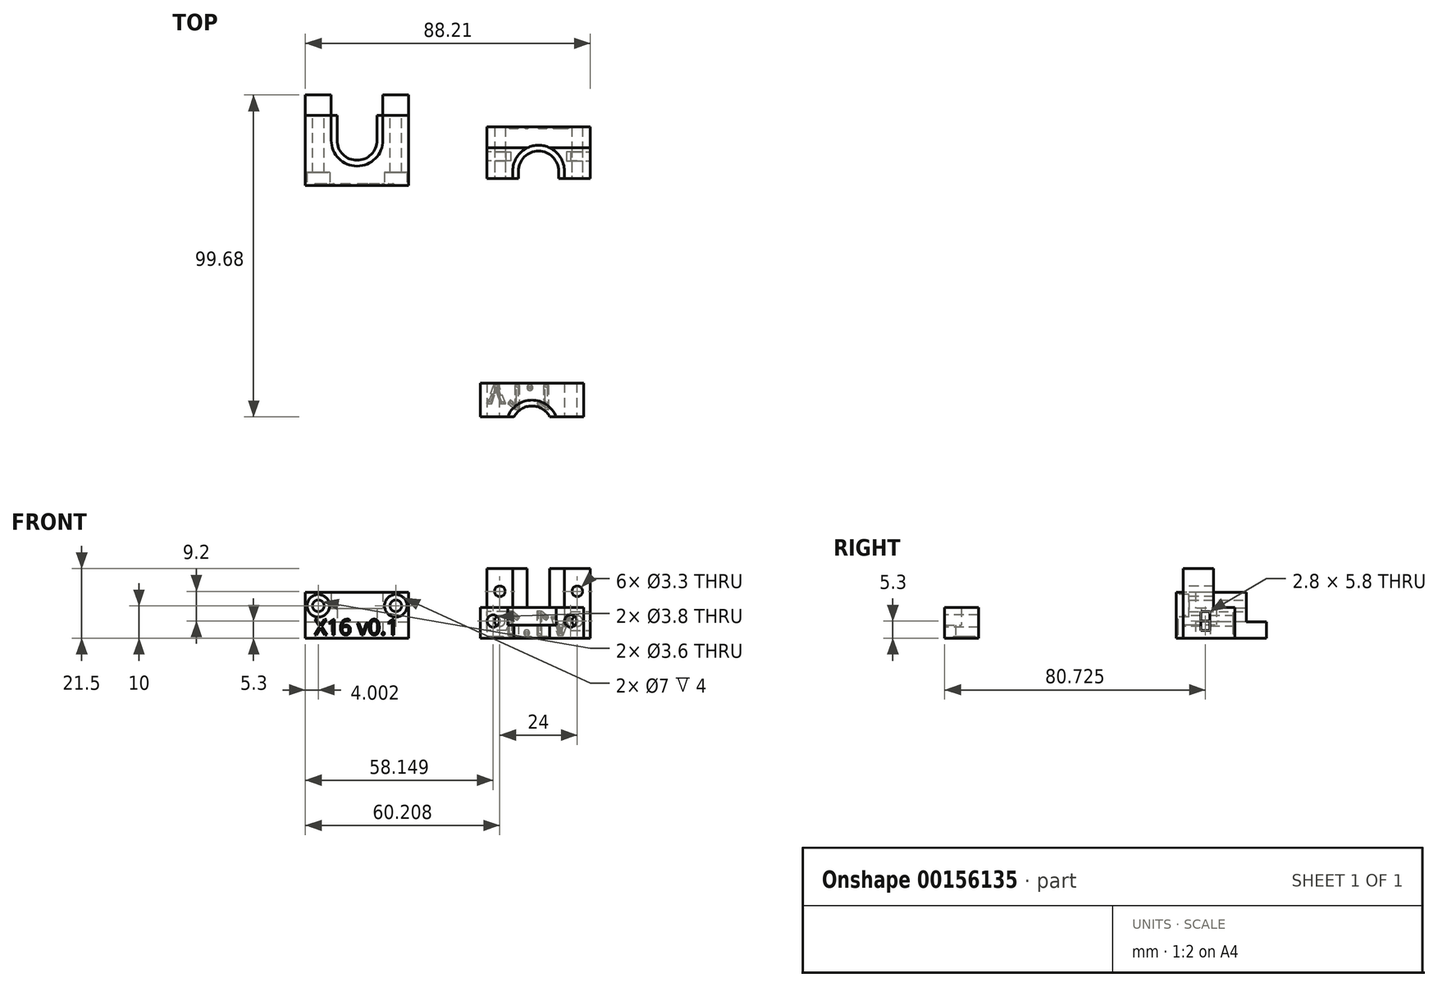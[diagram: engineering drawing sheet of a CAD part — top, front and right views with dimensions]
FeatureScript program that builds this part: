
annotation { "Feature Type Name" : "Feature", "Feature Type Description" : "" }
export const myFeature = defineFeature(function(context is Context, id is Id, definition is map)
    precondition{}
    {
        {
            var Q0;
            Q0=qCreatedBy(makeId("Top.planeOp"),FACE);
            var sketch = newSketch(context, id + "F0", { "sketchPlane" : qUnion([Q0])});
            skLineSegment(sketch, "E0.top", {"start": v(-38.58, -28.92) * mm, "end": v(-6.58, -28.92) * mm});
            skLineSegment(sketch, "E0.left", {"start": v(-38.58, -0.92) * mm, "end": v(-38.58, -28.92) * mm});
            skLineSegment(sketch, "E0.right", {"start": v(-6.58, -0.92) * mm, "end": v(-6.58, -28.92) * mm});
            skLineSegment(sketch, "E1", {"start": v(-38.58, -0.92) * mm, "end": v(-30.58, -0.92) * mm});
            skLineSegment(sketch, "E2", {"start": v(-14.58, -0.92) * mm, "end": v(-6.58, -0.92) * mm});
            skLineSegment(sketch, "E3.top", {"start": v(-22.58, -22.92) * mm, "end": v(-22.58, -22.92) * mm});
            skLineSegment(sketch, "E3.left", {"start": v(-30.58, -0.92) * mm, "end": v(-30.58, -14.92) * mm});
            skLineSegment(sketch, "E3.right", {"start": v(-14.58, -0.92) * mm, "end": v(-14.58, -14.92) * mm});
            skPoint(sketch, "E4.visualSharp", {"position": v(-30.58, -22.92) * mm});
            skArc(sketch, "E4.filletArc", {"start": v(-30.58, -14.92) * mm, "mid": v(-28.24, -20.58) * mm, "end": v(-22.58, -22.92) * mm});
            skPoint(sketch, "E5.visualSharp", {"position": v(-14.58, -22.92) * mm});
            skArc(sketch, "E5.filletArc", {"start": v(-22.58, -22.92) * mm, "mid": v(-16.92, -20.58) * mm, "end": v(-14.58, -14.92) * mm});
            skSolve(sketch);
        }
        {
            var Q0;
            Q0 = qSketchRegion(id + "F0", true);
            extrude(context, id + "F1", {"entities" : qUnion([Q0]), "depth" : 5 * mm});
        }
        {
            var Q0;
            Q0=makeQuery(id+"F1.opExtrude","CAP_FACE",FACE,{"disambiguationData":[OSD([sQuery(id+"F0.wireOp",EDGE,"E0.top"),sQuery(id+"F0.wireOp",EDGE,"E0.left"),sQuery(id+"F0.wireOp",EDGE,"E0.right"),sQuery(id+"F0.wireOp",EDGE,"E1"),sQuery(id+"F0.wireOp",EDGE,"E2"),sQuery(id+"F0.wireOp",EDGE,"E3.left"),sQuery(id+"F0.wireOp",EDGE,"E3.right"),sQuery(id+"F0.wireOp",EDGE,"E4.filletArc"),sQuery(id+"F0.wireOp",EDGE,"E5.filletArc")])],"isStart":false});
            var sketch = newSketch(context, id + "F2", { "sketchPlane" : qUnion([Q0])});
            skLineSegment(sketch, "E6", {"start": v(-6.58, -28.92) * mm, "end": v(-6.58, -7.22) * mm});
            skLineSegment(sketch, "E7", {"start": v(-6.58, -28.92) * mm, "end": v(-38.58, -28.92) * mm});
            skLineSegment(sketch, "E8", {"start": v(-38.58, -28.92) * mm, "end": v(-38.58, -7.22) * mm});
            skPoint(sketch, "E9.orphan", {"position": v(-30.58, -0.92) * mm});
            skPoint(sketch, "E10.orphan", {"position": v(-14.58, -0.92) * mm});
            skLineSegment(sketch, "E11", {"start": v(-38.58, -7.22) * mm, "end": v(-28.78, -7.22) * mm});
            skLineSegment(sketch, "E12", {"start": v(-16.38, -7.22) * mm, "end": v(-6.58, -7.22) * mm});
            skLineSegment(sketch, "E13.left", {"start": v(-28.78, -7.22) * mm, "end": v(-28.78, -14.92) * mm});
            skLineSegment(sketch, "E13.right", {"start": v(-16.38, -7.22) * mm, "end": v(-16.38, -14.92) * mm});
            skArc(sketch, "E14", {"start": v(-28.78, -14.92) * mm, "mid": v(-22.58, -21.12) * mm, "end": v(-16.38, -14.92) * mm});
            skSolve(sketch);
        }
        {
            var Q0;
            Q0 = qSketchRegion(id + "F2", true);
            extrude(context, id + "F3", {"entities" : qUnion([Q0]), "operationType" : NewBodyOperationType.ADD, "depth" : 4.2 * mm});
        }
        {
            var Q0;
            Q0=makeQuery(id+"F3.opExtrude","CAP_FACE",FACE,{"disambiguationData":[OSD([sQuery(id+"F2.wireOp",EDGE,"E6"),sQuery(id+"F2.wireOp",EDGE,"E7"),sQuery(id+"F2.wireOp",EDGE,"E8"),sQuery(id+"F2.wireOp",EDGE,"E11"),sQuery(id+"F2.wireOp",EDGE,"E12"),sQuery(id+"F2.wireOp",EDGE,"E13.left"),sQuery(id+"F2.wireOp",EDGE,"E13.right"),sQuery(id+"F2.wireOp",EDGE,"E14")])],"isStart":false});
            var sketch = newSketch(context, id + "F4", { "sketchPlane" : qUnion([Q0])});
            skLineSegment(sketch, "E15.0", {"start": v(-38.58, -7.22) * mm, "end": v(-38.58, -28.92) * mm});
            skLineSegment(sketch, "E16.0", {"start": v(-38.58, -28.92) * mm, "end": v(-6.58, -28.92) * mm});
            skLineSegment(sketch, "E17.0", {"start": v(-6.58, -7.22) * mm, "end": v(-6.58, -28.92) * mm});
            skPoint(sketch, "E18.orphan", {"position": v(-38.58, -0.92) * mm});
            skPoint(sketch, "E19.orphan", {"position": v(-6.58, -0.92) * mm});
            skPoint(sketch, "E20.0.start.orphan", {"position": v(-28.78, -14.92) * mm});
            skPoint(sketch, "E21.0.end.orphan", {"position": v(-16.38, -14.92) * mm});
            skPoint(sketch, "E22.0.start.orphan", {"position": v(-16.38, -7.22) * mm});
            skPoint(sketch, "E23.0.end.orphan", {"position": v(-28.78, -7.22) * mm});
            skLineSegment(sketch, "E24.0", {"start": v(-30.58, -7.22) * mm, "end": v(-30.58, -14.92) * mm});
            skLineSegment(sketch, "E25.0", {"start": v(-14.58, -7.22) * mm, "end": v(-14.58, -14.92) * mm});
            skArc(sketch, "E26.0", {"start": v(-22.58, -22.92) * mm, "mid": v(-16.92, -20.58) * mm, "end": v(-14.58, -14.92) * mm});
            skArc(sketch, "E27.0", {"start": v(-30.58, -14.92) * mm, "mid": v(-28.24, -20.58) * mm, "end": v(-22.58, -22.92) * mm});
            skLineSegment(sketch, "E28", {"start": v(-38.58, -7.22) * mm, "end": v(-30.58, -7.22) * mm});
            skLineSegment(sketch, "E29", {"start": v(-6.58, -7.22) * mm, "end": v(-14.58, -7.22) * mm});
            skPoint(sketch, "E30.orphan", {"position": v(-30.58, -0.92) * mm});
            skPoint(sketch, "E31.orphan", {"position": v(-14.58, -0.92) * mm});
            skSolve(sketch);
        }
        {
            var Q0;
            Q0 = qSketchRegion(id + "F4", true);
            extrude(context, id + "F5", {"entities" : qUnion([Q0]), "operationType" : NewBodyOperationType.ADD, "depth" : 5 * mm});
        }
        {
            var Q0;
            Q0=makeQuery(id+"F5.boolean.opBoolean","MERGE",FACE,{"derivedFrom":[makeQuery(id+"F3.opExtrude","SWEPT_FACE",FACE,{"disambiguationData":[OSD([sQuery(id+"F2.wireOp",EDGE,"E12")])]}),makeQuery(id+"F5.opExtrude","SWEPT_FACE",FACE,{"disambiguationData":[OSD([sQuery(id+"F4.wireOp",EDGE,"E29")])]})]});
            var sketch = newSketch(context, id + "F6", { "sketchPlane" : qUnion([Q0])});
            skLineSegment(sketch, "E32.0", {"start": v(14.58, 0) * mm, "end": v(6.58, 0) * mm});
            skLineSegment(sketch, "E33", {"start": v(6.58, 0) * mm, "end": v(6.58, 10) * mm});
            skLineSegment(sketch, "E34.0", {"start": v(38.58, 0) * mm, "end": v(30.58, 0) * mm});
            skLineSegment(sketch, "E35", {"start": v(30.58, 0) * mm, "end": v(30.58, 10) * mm});
            skLineSegment(sketch, "E36", {"start": v(6.58, 10) * mm, "end": v(10.58, 10) * mm});
            skLineSegment(sketch, "E37", {"start": v(30.58, 10) * mm, "end": v(34.58, 10) * mm});
            skCircle(sketch, "E38", {"center": v(10.58, 10) * mm, "radius": 1.8 * mm});
            skCircle(sketch, "E39", {"center": v(34.58, 10) * mm, "radius": 1.8 * mm});
            skSolve(sketch);
        }
        {
            var Q0;
            Q0 = qSketchRegion(id + "F6", true);
            extrude(context, id + "F7", {"entities" : qUnion([Q0]), "operationType" : NewBodyOperationType.REMOVE, "oppositeDirection" : true, "depth" : 25 * mm});
        }
        {
            var Q0;
            Q0=qCreatedBy(makeId("Top.planeOp"),FACE);
            var sketch = newSketch(context, id + "F8", { "sketchPlane" : qUnion([Q0])});
            skLineSegment(sketch, "E40.bottom", {"start": v(17.63, -10.78) * mm, "end": v(49.63, -10.78) * mm});
            skLineSegment(sketch, "E40.left", {"start": v(17.63, -10.78) * mm, "end": v(17.63, -26.78) * mm});
            skLineSegment(sketch, "E40.right", {"start": v(49.63, -10.78) * mm, "end": v(49.63, -26.78) * mm});
            skLineSegment(sketch, "E41", {"start": v(17.63, -26.78) * mm, "end": v(27.43, -26.78) * mm});
            skLineSegment(sketch, "E42", {"start": v(49.63, -26.78) * mm, "end": v(39.83, -26.78) * mm});
            skLineSegment(sketch, "E43", {"start": v(27.43, -26.78) * mm, "end": v(27.43, -24.48) * mm});
            skLineSegment(sketch, "E44", {"start": v(39.83, -26.78) * mm, "end": v(39.83, -24.48) * mm});
            skArc(sketch, "E45", {"start": v(39.83, -24.48) * mm, "mid": v(33.63, -18.28) * mm, "end": v(27.43, -24.48) * mm});
            skSolve(sketch);
        }
        {
            var Q0;
            Q0 = qSketchRegion(id + "F8", true);
            extrude(context, id + "F9", {"entities" : qUnion([Q0]), "depth" : 4.2 * mm});
        }
        {
            var Q0;
            Q0=makeQuery(id+"F9.opExtrude","CAP_FACE",FACE,{"disambiguationData":[OSD([sQuery(id+"F8.wireOp",EDGE,"E40.bottom"),sQuery(id+"F8.wireOp",EDGE,"E40.left"),sQuery(id+"F8.wireOp",EDGE,"E40.right"),sQuery(id+"F8.wireOp",EDGE,"E41"),sQuery(id+"F8.wireOp",EDGE,"E42"),sQuery(id+"F8.wireOp",EDGE,"E43"),sQuery(id+"F8.wireOp",EDGE,"E44"),sQuery(id+"F8.wireOp",EDGE,"E45")])],"isStart":false});
            var sketch = newSketch(context, id + "F10", { "sketchPlane" : qUnion([Q0])});
            skLineSegment(sketch, "E46", {"start": v(49.63, -26.78) * mm, "end": v(41.63, -26.78) * mm});
            skLineSegment(sketch, "E47", {"start": v(41.63, -26.78) * mm, "end": v(41.63, -24.48) * mm});
            skLineSegment(sketch, "E48", {"start": v(17.63, -26.78) * mm, "end": v(25.63, -26.78) * mm});
            skLineSegment(sketch, "E49", {"start": v(25.63, -26.78) * mm, "end": v(25.63, -24.48) * mm});
            skArc(sketch, "E50", {"start": v(41.63, -24.48) * mm, "mid": v(33.63, -16.48) * mm, "end": v(25.63, -24.48) * mm});
            skLineSegment(sketch, "E51.0", {"start": v(17.63, -10.78) * mm, "end": v(17.63, -26.78) * mm});
            skLineSegment(sketch, "E52.0", {"start": v(17.63, -10.78) * mm, "end": v(49.63, -10.78) * mm});
            skLineSegment(sketch, "E53.0", {"start": v(49.63, -10.78) * mm, "end": v(49.63, -26.78) * mm});
            skSolve(sketch);
        }
        {
            var Q0;
            Q0 = qSketchRegion(id + "F10", true);
            extrude(context, id + "F11", {"entities" : qUnion([Q0]), "operationType" : NewBodyOperationType.ADD, "depth" : 17.3 * mm});
        }
        {
            var Q0;
            Q0=makeQuery(id+"F11.opExtrude","CAP_FACE",FACE,{"disambiguationData":[OSD([sQuery(id+"F10.wireOp",EDGE,"E46"),sQuery(id+"F10.wireOp",EDGE,"E47"),sQuery(id+"F10.wireOp",EDGE,"E48"),sQuery(id+"F10.wireOp",EDGE,"E49"),sQuery(id+"F10.wireOp",EDGE,"E50"),sQuery(id+"F10.wireOp",EDGE,"E51.0"),sQuery(id+"F10.wireOp",EDGE,"E52.0"),sQuery(id+"F10.wireOp",EDGE,"E53.0")])],"isStart":false});
            var sketch = newSketch(context, id + "F12", { "sketchPlane" : qUnion([Q0])});
            skLineSegment(sketch, "E54.bottom", {"start": v(17.63, -10.78) * mm, "end": v(49.63, -10.78) * mm});
            skLineSegment(sketch, "E54.top", {"start": v(17.63, -17.28) * mm, "end": v(49.63, -17.28) * mm});
            skLineSegment(sketch, "E54.left", {"start": v(17.63, -10.78) * mm, "end": v(17.63, -17.28) * mm});
            skLineSegment(sketch, "E54.right", {"start": v(49.63, -10.78) * mm, "end": v(49.63, -17.28) * mm});
            skSolve(sketch);
        }
        {
            var Q0;
            Q0 = qSketchRegion(id + "F12", true);
            extrude(context, id + "F13", {"entities" : qUnion([Q0]), "operationType" : NewBodyOperationType.REMOVE, "oppositeDirection" : true, "depth" : 12 * mm});
        }
        {
            var Q0;
            Q0=makeQuery(id+"F11.boolean.opBoolean","MERGE",FACE,{"derivedFrom":[makeQuery(id+"F9.opExtrude","SWEPT_FACE",FACE,{"disambiguationData":[OSD([sQuery(id+"F8.wireOp",EDGE,"E41")])]}),makeQuery(id+"F11.opExtrude","SWEPT_FACE",FACE,{"disambiguationData":[OSD([sQuery(id+"F10.wireOp",EDGE,"E48")])]})]});
            var sketch = newSketch(context, id + "F14", { "sketchPlane" : qUnion([Q0])});
            skLineSegment(sketch, "E55", {"start": v(17.63, 21.5) * mm, "end": v(17.63, 14.5) * mm, "construction": true});
            skLineSegment(sketch, "E56", {"start": v(17.63, 14.5) * mm, "end": v(21.63, 14.5) * mm, "construction": true});
            skLineSegment(sketch, "E57", {"start": v(21.63, 14.5) * mm, "end": v(45.63, 14.5) * mm, "construction": true});
            skLineSegment(sketch, "E58.0", {"start": v(49.63, 21.5) * mm, "end": v(49.63, 0) * mm, "construction": true});
            skLineSegment(sketch, "E59", {"start": v(45.63, 14.5) * mm, "end": v(49.63, 14.5) * mm, "construction": true});
            skLineSegment(sketch, "E60", {"start": v(45.63, 14.5) * mm, "end": v(45.63, 5.3) * mm, "construction": true});
            skLineSegment(sketch, "E61", {"start": v(45.63, 5.3) * mm, "end": v(21.63, 5.3) * mm, "construction": true});
            skCircle(sketch, "E62", {"center": v(21.63, 14.5) * mm, "radius": 1.65 * mm});
            skCircle(sketch, "E63", {"center": v(45.63, 14.5) * mm, "radius": 1.65 * mm});
            skCircle(sketch, "E64", {"center": v(45.63, 5.3) * mm, "radius": 1.65 * mm});
            skCircle(sketch, "E65", {"center": v(21.63, 5.3) * mm, "radius": 1.65 * mm});
            skSolve(sketch);
        }
        {
            var Q0;
            Q0 = qSketchRegion(id + "F14", true);
            extrude(context, id + "F15", {"entities" : qUnion([Q0]), "operationType" : NewBodyOperationType.REMOVE, "oppositeDirection" : true, "depth" : 25 * mm});
        }
        {
            var Q0;
            Q0=makeQuery(id+"F11.boolean.opBoolean","MERGE",FACE,{"derivedFrom":[makeQuery(id+"F9.opExtrude","SWEPT_FACE",FACE,{"disambiguationData":[OSD([sQuery(id+"F8.wireOp",EDGE,"E40.left")])]}),makeQuery(id+"F11.opExtrude","SWEPT_FACE",FACE,{"disambiguationData":[OSD([sQuery(id+"F10.wireOp",EDGE,"E51.0")])]})]});
            var sketch = newSketch(context, id + "F16", { "sketchPlane" : qUnion([Q0])});
            skLineSegment(sketch, "E66", {"start": v(26.78, 0) * mm, "end": v(21.28, 0) * mm});
            skLineSegment(sketch, "E67", {"start": v(21.28, 0) * mm, "end": v(21.28, 2.4) * mm});
            skLineSegment(sketch, "E68.bottom", {"start": v(21.28, 2.4) * mm, "end": v(18.48, 2.4) * mm});
            skLineSegment(sketch, "E68.top", {"start": v(21.28, 8.2) * mm, "end": v(18.48, 8.2) * mm});
            skLineSegment(sketch, "E68.left", {"start": v(21.28, 2.4) * mm, "end": v(21.28, 8.2) * mm});
            skLineSegment(sketch, "E68.right", {"start": v(18.48, 2.4) * mm, "end": v(18.48, 8.2) * mm});
            skSolve(sketch);
        }
        {
            var Q0;
            Q0 = qSketchRegion(id + "F16", true);
            extrude(context, id + "F17", {"entities" : qUnion([Q0]), "operationType" : NewBodyOperationType.REMOVE, "oppositeDirection" : true, "depth" : 6 * mm});
        }
        {
            var Q0;
            Q0=makeQuery(id+"F11.boolean.opBoolean","MERGE",FACE,{"derivedFrom":[makeQuery(id+"F9.opExtrude","SWEPT_FACE",FACE,{"disambiguationData":[OSD([sQuery(id+"F8.wireOp",EDGE,"E40.right")])]}),makeQuery(id+"F11.opExtrude","SWEPT_FACE",FACE,{"disambiguationData":[OSD([sQuery(id+"F10.wireOp",EDGE,"E53.0")])]})]});
            var sketch = newSketch(context, id + "F18", { "sketchPlane" : qUnion([Q0])});
            skLineSegment(sketch, "E69.0", {"start": v(-21.28, 8.2) * mm, "end": v(-18.48, 8.2) * mm});
            skLineSegment(sketch, "E70.0", {"start": v(-21.28, 2.4) * mm, "end": v(-21.28, 8.2) * mm});
            skLineSegment(sketch, "E71.0", {"start": v(-21.28, 2.4) * mm, "end": v(-18.48, 2.4) * mm});
            skLineSegment(sketch, "E72.0", {"start": v(-18.48, 2.4) * mm, "end": v(-18.48, 8.2) * mm});
            skSolve(sketch);
        }
        {
            var Q0;
            Q0 = qSketchRegion(id + "F18", true);
            extrude(context, id + "F19", {"entities" : qUnion([Q0]), "operationType" : NewBodyOperationType.REMOVE, "oppositeDirection" : true, "depth" : 6 * mm});
        }
        {
            var Q0;
            Q0=makeQuery(id+"F17.boolean.opBoolean","COPY",FACE,{"derivedFrom":makeQuery(id+"F17.opExtrude","SWEPT_FACE",FACE,{"disambiguationData":[OSD([sQuery(id+"F16.wireOp",EDGE,"E68.left")])]})});
            var sketch = newSketch(context, id + "F20", { "sketchPlane" : qUnion([Q0])});
            skLineSegment(sketch, "E73", {"start": v(-23.63, 8.2) * mm, "end": v(-23.63, 2.4) * mm});
            skLineSegment(sketch, "E74", {"start": v(-23.63, 2.4) * mm, "end": v(-24.98, 5.3) * mm});
            skLineSegment(sketch, "E75", {"start": v(-24.98, 5.3) * mm, "end": v(-23.63, 8.2) * mm});
            skLineSegment(sketch, "E76.0", {"start": v(-43.63, 2.4) * mm, "end": v(-43.63, 8.2) * mm});
            skLineSegment(sketch, "E77", {"start": v(-43.63, 8.2) * mm, "end": v(-42.27, 5.3) * mm});
            skLineSegment(sketch, "E78", {"start": v(-42.27, 5.3) * mm, "end": v(-43.63, 2.4) * mm});
            skSolve(sketch);
        }
        {
            var Q0;
            Q0 = qSketchRegion(id + "F20", true);
            extrude(context, id + "F21", {"entities" : qUnion([Q0]), "operationType" : NewBodyOperationType.REMOVE, "depth" : 2.8 * mm});
        }
        {
            var Q0;
            Q0=makeQuery(id+"F11.boolean.opBoolean","MERGE",FACE,{"derivedFrom":[makeQuery(id+"F9.opExtrude","SWEPT_FACE",FACE,{"disambiguationData":[OSD([sQuery(id+"F8.wireOp",EDGE,"E40.bottom")])]}),makeQuery(id+"F11.opExtrude","SWEPT_FACE",FACE,{"disambiguationData":[OSD([sQuery(id+"F10.wireOp",EDGE,"E52.0")])]})]});
            var sketch = newSketch(context, id + "F22", { "sketchPlane" : qUnion([Q0])});
            skText(sketch, "E79", { "text": "v1.1", "fontName": "OpenSans-Bold.ttf"});
            const initialGuessF22  = {"E79": [-0.04342, 0.00088, 1, 0, 0.00757]};
            skSetInitialGuess(sketch, initialGuessF22);
            skSolve(sketch);
        }
        {
            var Q0;
            Q0 = qSketchRegion(id + "F22", true);
            extrude(context, id + "F23", {"entities" : qUnion([Q0]), "operationType" : NewBodyOperationType.REMOVE, "oppositeDirection" : true, "depth" : .5 * mm});
        }
        {
            var Q0;
            Q0=qCreatedBy(makeId("Top.planeOp"),FACE);
            var sketch = newSketch(context, id + "F24", { "sketchPlane" : qUnion([Q0])});
            skLineSegment(sketch, "E80.bottom", {"start": v(15.57, -90.1) * mm, "end": v(47.57, -90.1) * mm});
            skLineSegment(sketch, "E80.top", {"start": v(15.57, -100.6) * mm, "end": v(26.04, -100.6) * mm});
            skLineSegment(sketch, "E80.left", {"start": v(15.57, -90.1) * mm, "end": v(15.57, -100.6) * mm});
            skLineSegment(sketch, "E80.right", {"start": v(47.57, -90.1) * mm, "end": v(47.57, -100.6) * mm});
            skArc(sketch, "E81", {"start": v(37.1, -100.6) * mm, "mid": v(31.57, -97.2) * mm, "end": v(26.04, -100.6) * mm});
            skLineSegment(sketch, "E82.trimOffspring", {"start": v(37.1, -100.6) * mm, "end": v(47.57, -100.6) * mm});
            skPoint(sketch, "E83.start.orphan", {"position": v(31.57, -100.6) * mm});
            skSolve(sketch);
        }
        {
            var Q0;
            Q0 = qSketchRegion(id + "F24", true);
            extrude(context, id + "F25", {"entities" : qUnion([Q0]), "depth" : 4 * mm});
        }
        {
            var Q0;
            Q0=makeQuery(id+"F25.opExtrude","CAP_FACE",FACE,{"disambiguationData":[OSD([sQuery(id+"F24.wireOp",EDGE,"E80.bottom"),sQuery(id+"F24.wireOp",EDGE,"E80.top"),sQuery(id+"F24.wireOp",EDGE,"E80.left"),sQuery(id+"F24.wireOp",EDGE,"E80.right"),sQuery(id+"F24.wireOp",EDGE,"E81"),sQuery(id+"F24.wireOp",EDGE,"E82.trimOffspring")])],"isStart":false});
            var sketch = newSketch(context, id + "F26", { "sketchPlane" : qUnion([Q0])});
            skLineSegment(sketch, "E84.0", {"start": v(15.57, -90.1) * mm, "end": v(47.57, -90.1) * mm});
            skLineSegment(sketch, "E85.0", {"start": v(15.57, -90.1) * mm, "end": v(15.57, -100.6) * mm});
            skLineSegment(sketch, "E86.0", {"start": v(47.57, -90.1) * mm, "end": v(47.57, -100.6) * mm});
            skPoint(sketch, "E87.0", {"position": v(31.57, -103.4) * mm});
            skArc(sketch, "E88", {"start": v(39.06, -100.6) * mm, "mid": v(31.57, -95.4) * mm, "end": v(24.07, -100.6) * mm});
            skLineSegment(sketch, "E89", {"start": v(15.57, -100.6) * mm, "end": v(24.07, -100.6) * mm});
            skLineSegment(sketch, "E90", {"start": v(47.57, -100.6) * mm, "end": v(39.06, -100.6) * mm});
            skSolve(sketch);
        }
        {
            var Q0;
            Q0 = qSketchRegion(id + "F26", true);
            extrude(context, id + "F27", {"entities" : qUnion([Q0]), "operationType" : NewBodyOperationType.ADD, "depth" : 5.5 * mm});
        }
        {
            var Q0;
            Q0=makeQuery(id+"F27.boolean.opBoolean","MERGE",FACE,{"derivedFrom":[makeQuery(id+"F25.opExtrude","SWEPT_FACE",FACE,{"disambiguationData":[OSD([sQuery(id+"F24.wireOp",EDGE,"E80.top")])]}),makeQuery(id+"F27.opExtrude","SWEPT_FACE",FACE,{"disambiguationData":[OSD([sQuery(id+"F26.wireOp",EDGE,"E89")])]})]});
            var sketch = newSketch(context, id + "F28", { "sketchPlane" : qUnion([Q0])});
            skLineSegment(sketch, "E91", {"start": v(15.57, 9.5) * mm, "end": v(15.57, 5.3) * mm, "construction": true});
            skLineSegment(sketch, "E92", {"start": v(15.57, 5.3) * mm, "end": v(19.57, 5.3) * mm, "construction": true});
            skLineSegment(sketch, "E93", {"start": v(19.57, 5.3) * mm, "end": v(43.57, 5.3) * mm, "construction": true});
            skCircle(sketch, "E94", {"center": v(19.57, 5.3) * mm, "radius": 1.9 * mm});
            skCircle(sketch, "E95", {"center": v(43.57, 5.3) * mm, "radius": 1.9 * mm});
            skSolve(sketch);
        }
        {
            var Q0;
            Q0 = qSketchRegion(id + "F28", true);
            extrude(context, id + "F29", {"entities" : qUnion([Q0]), "operationType" : NewBodyOperationType.REMOVE, "oppositeDirection" : true, "depth" : 25 * mm});
        }
        {
            var Q0;
            Q0=makeQuery(id+"F25.opExtrude","CAP_FACE",FACE,{"disambiguationData":[OSD([sQuery(id+"F24.wireOp",EDGE,"E80.bottom"),sQuery(id+"F24.wireOp",EDGE,"E80.top"),sQuery(id+"F24.wireOp",EDGE,"E80.left"),sQuery(id+"F24.wireOp",EDGE,"E80.right"),sQuery(id+"F24.wireOp",EDGE,"E81"),sQuery(id+"F24.wireOp",EDGE,"E82.trimOffspring")])],"isStart":true});
            var sketch = newSketch(context, id + "F30", { "sketchPlane" : qUnion([Q0])});
            skText(sketch, "E96", { "text": "v1.1", "fontName": "OpenSans-Bold.ttf"});
            const initialGuessF30  = {"E96": [0.01747, 0.09077, 1, 0, 0.00757]};
            skSetInitialGuess(sketch, initialGuessF30);
            skSolve(sketch);
        }
        {
            var Q0;
            Q0 = qSketchRegion(id + "F30", true);
            extrude(context, id + "F31", {"entities" : qUnion([Q0]), "operationType" : NewBodyOperationType.REMOVE, "oppositeDirection" : true, "depth" : .5 * mm});
        }
        {
            var Q0;
            Q0=makeQuery(id+"F31.boolean.opBoolean","COPY",FACE,{"derivedFrom":makeQuery(id+"F31.opExtrude","CAP_FACE",FACE,{"disambiguationData":[OSD([sQuery(id+"F30.wireOp",EDGE,"E96.sketch_text.stroke-0"),sQuery(id+"F30.wireOp",EDGE,"E96.sketch_text.stroke-1"),sQuery(id+"F30.wireOp",EDGE,"E96.sketch_text.stroke-2"),sQuery(id+"F30.wireOp",EDGE,"E96.sketch_text.stroke-3"),sQuery(id+"F30.wireOp",EDGE,"E96.sketch_text.stroke-4"),sQuery(id+"F30.wireOp",EDGE,"E96.sketch_text.stroke-5"),sQuery(id+"F30.wireOp",EDGE,"E96.sketch_text.stroke-6"),sQuery(id+"F30.wireOp",EDGE,"E96.sketch_text.stroke-7"),sQuery(id+"F30.wireOp",EDGE,"E96.sketch_text.stroke-8"),sQuery(id+"F30.wireOp",EDGE,"E96.sketch_text.stroke-9")])],"isStart":false})});
            var Q1;
            Q1=makeQuery(id+"F31.boolean.opBoolean","COPY",FACE,{"derivedFrom":makeQuery(id+"F31.opExtrude","CAP_FACE",FACE,{"disambiguationData":[OSD([sQuery(id+"F30.wireOp",EDGE,"E96.sketch_text.stroke-10"),sQuery(id+"F30.wireOp",EDGE,"E96.sketch_text.stroke-11"),sQuery(id+"F30.wireOp",EDGE,"E96.sketch_text.stroke-12"),sQuery(id+"F30.wireOp",EDGE,"E96.sketch_text.stroke-13"),sQuery(id+"F30.wireOp",EDGE,"E96.sketch_text.stroke-14"),sQuery(id+"F30.wireOp",EDGE,"E96.sketch_text.stroke-15"),sQuery(id+"F30.wireOp",EDGE,"E96.sketch_text.stroke-16"),sQuery(id+"F30.wireOp",EDGE,"E96.sketch_text.stroke-17"),sQuery(id+"F30.wireOp",EDGE,"E96.sketch_text.stroke-18"),sQuery(id+"F30.wireOp",EDGE,"E96.sketch_text.stroke-19")])],"isStart":false})});
            var Q2;
            Q2=makeQuery(id+"F31.boolean.opBoolean","COPY",FACE,{"derivedFrom":makeQuery(id+"F31.opExtrude","CAP_FACE",FACE,{"disambiguationData":[OSD([sQuery(id+"F30.wireOp",EDGE,"E96.sketch_text.stroke-20"),sQuery(id+"F30.wireOp",EDGE,"E96.sketch_text.stroke-21"),sQuery(id+"F30.wireOp",EDGE,"E96.sketch_text.stroke-22"),sQuery(id+"F30.wireOp",EDGE,"E96.sketch_text.stroke-23"),sQuery(id+"F30.wireOp",EDGE,"E96.sketch_text.stroke-24"),sQuery(id+"F30.wireOp",EDGE,"E96.sketch_text.stroke-25"),sQuery(id+"F30.wireOp",EDGE,"E96.sketch_text.stroke-26"),sQuery(id+"F30.wireOp",EDGE,"E96.sketch_text.stroke-27")])],"isStart":false})});
            var Q3;
            Q3=makeQuery(id+"F31.boolean.opBoolean","COPY",FACE,{"derivedFrom":makeQuery(id+"F31.opExtrude","CAP_FACE",FACE,{"disambiguationData":[OSD([sQuery(id+"F30.wireOp",EDGE,"E96.sketch_text.stroke-28"),sQuery(id+"F30.wireOp",EDGE,"E96.sketch_text.stroke-29"),sQuery(id+"F30.wireOp",EDGE,"E96.sketch_text.stroke-30"),sQuery(id+"F30.wireOp",EDGE,"E96.sketch_text.stroke-31"),sQuery(id+"F30.wireOp",EDGE,"E96.sketch_text.stroke-32"),sQuery(id+"F30.wireOp",EDGE,"E96.sketch_text.stroke-33"),sQuery(id+"F30.wireOp",EDGE,"E96.sketch_text.stroke-34"),sQuery(id+"F30.wireOp",EDGE,"E96.sketch_text.stroke-35"),sQuery(id+"F30.wireOp",EDGE,"E96.sketch_text.stroke-36"),sQuery(id+"F30.wireOp",EDGE,"E96.sketch_text.stroke-37"),sQuery(id+"F30.wireOp",EDGE,"E96.sketch_text.stroke-38"),sQuery(id+"F30.wireOp",EDGE,"E96.sketch_text.stroke-39"),sQuery(id+"F30.wireOp",EDGE,"E96.sketch_text.stroke-40"),sQuery(id+"F30.wireOp",EDGE,"E96.sketch_text.stroke-41"),sQuery(id+"F30.wireOp",EDGE,"E96.sketch_text.stroke-42"),sQuery(id+"F30.wireOp",EDGE,"E96.sketch_text.stroke-43")])],"isStart":false})});
            chamfer(context, id + "F32", {"entities" : qUnion([Q0, Q1, Q2, Q3]), "width" : .5 * mm, "tangentPropagation" : true});
        }
        {
            var Q0;
            Q0=makeQuery(id+"F23.boolean.opBoolean","COPY",FACE,{"derivedFrom":makeQuery(id+"F23.opExtrude","CAP_FACE",FACE,{"disambiguationData":[OSD([sQuery(id+"F22.wireOp",EDGE,"E79.sketch_text.stroke-0"),sQuery(id+"F22.wireOp",EDGE,"E79.sketch_text.stroke-1"),sQuery(id+"F22.wireOp",EDGE,"E79.sketch_text.stroke-2"),sQuery(id+"F22.wireOp",EDGE,"E79.sketch_text.stroke-3"),sQuery(id+"F22.wireOp",EDGE,"E79.sketch_text.stroke-4"),sQuery(id+"F22.wireOp",EDGE,"E79.sketch_text.stroke-5"),sQuery(id+"F22.wireOp",EDGE,"E79.sketch_text.stroke-6"),sQuery(id+"F22.wireOp",EDGE,"E79.sketch_text.stroke-7"),sQuery(id+"F22.wireOp",EDGE,"E79.sketch_text.stroke-8"),sQuery(id+"F22.wireOp",EDGE,"E79.sketch_text.stroke-9")])],"isStart":false})});
            var Q1;
            Q1=makeQuery(id+"F23.boolean.opBoolean","COPY",FACE,{"derivedFrom":makeQuery(id+"F23.opExtrude","CAP_FACE",FACE,{"disambiguationData":[OSD([sQuery(id+"F22.wireOp",EDGE,"E79.sketch_text.stroke-10"),sQuery(id+"F22.wireOp",EDGE,"E79.sketch_text.stroke-11"),sQuery(id+"F22.wireOp",EDGE,"E79.sketch_text.stroke-12"),sQuery(id+"F22.wireOp",EDGE,"E79.sketch_text.stroke-13"),sQuery(id+"F22.wireOp",EDGE,"E79.sketch_text.stroke-14"),sQuery(id+"F22.wireOp",EDGE,"E79.sketch_text.stroke-15"),sQuery(id+"F22.wireOp",EDGE,"E79.sketch_text.stroke-16"),sQuery(id+"F22.wireOp",EDGE,"E79.sketch_text.stroke-17"),sQuery(id+"F22.wireOp",EDGE,"E79.sketch_text.stroke-18"),sQuery(id+"F22.wireOp",EDGE,"E79.sketch_text.stroke-19")])],"isStart":false})});
            var Q2;
            Q2=makeQuery(id+"F23.boolean.opBoolean","COPY",FACE,{"derivedFrom":makeQuery(id+"F23.opExtrude","CAP_FACE",FACE,{"disambiguationData":[OSD([sQuery(id+"F22.wireOp",EDGE,"E79.sketch_text.stroke-20"),sQuery(id+"F22.wireOp",EDGE,"E79.sketch_text.stroke-21"),sQuery(id+"F22.wireOp",EDGE,"E79.sketch_text.stroke-22"),sQuery(id+"F22.wireOp",EDGE,"E79.sketch_text.stroke-23"),sQuery(id+"F22.wireOp",EDGE,"E79.sketch_text.stroke-24"),sQuery(id+"F22.wireOp",EDGE,"E79.sketch_text.stroke-25"),sQuery(id+"F22.wireOp",EDGE,"E79.sketch_text.stroke-26"),sQuery(id+"F22.wireOp",EDGE,"E79.sketch_text.stroke-27")])],"isStart":false})});
            var Q3;
            Q3=makeQuery(id+"F23.boolean.opBoolean","COPY",FACE,{"derivedFrom":makeQuery(id+"F23.opExtrude","CAP_FACE",FACE,{"disambiguationData":[OSD([sQuery(id+"F22.wireOp",EDGE,"E79.sketch_text.stroke-28"),sQuery(id+"F22.wireOp",EDGE,"E79.sketch_text.stroke-29"),sQuery(id+"F22.wireOp",EDGE,"E79.sketch_text.stroke-30"),sQuery(id+"F22.wireOp",EDGE,"E79.sketch_text.stroke-31"),sQuery(id+"F22.wireOp",EDGE,"E79.sketch_text.stroke-32"),sQuery(id+"F22.wireOp",EDGE,"E79.sketch_text.stroke-33"),sQuery(id+"F22.wireOp",EDGE,"E79.sketch_text.stroke-34"),sQuery(id+"F22.wireOp",EDGE,"E79.sketch_text.stroke-35"),sQuery(id+"F22.wireOp",EDGE,"E79.sketch_text.stroke-36"),sQuery(id+"F22.wireOp",EDGE,"E79.sketch_text.stroke-37")])],"isStart":false})});
            chamfer(context, id + "F33", {"entities" : qUnion([Q0, Q1, Q2, Q3]), "width" : .5 * mm, "tangentPropagation" : true});
        }
        {
            var Q0;
            Q0=makeQuery(id+"F5.boolean.opBoolean","MERGE",FACE,{"derivedFrom":[makeQuery(id+"F3.boolean.opBoolean","MERGE",FACE,{"derivedFrom":[makeQuery(id+"F1.opExtrude","SWEPT_FACE",FACE,{"disambiguationData":[OSD([sQuery(id+"F0.wireOp",EDGE,"E0.top")])]}),makeQuery(id+"F3.opExtrude","SWEPT_FACE",FACE,{"disambiguationData":[OSD([sQuery(id+"F2.wireOp",EDGE,"E7")])]})]}),makeQuery(id+"F5.opExtrude","SWEPT_FACE",FACE,{"disambiguationData":[OSD([sQuery(id+"F4.wireOp",EDGE,"E16.0")])]})]});
            var sketch = newSketch(context, id + "F34", { "sketchPlane" : qUnion([Q0])});
            skCircle(sketch, "E97", {"center": v(-34.58, 10) * mm, "radius": 3.5 * mm});
            skCircle(sketch, "E98", {"center": v(-10.58, 10) * mm, "radius": 3.5 * mm});
            skSolve(sketch);
        }
        {
            var Q0;
            Q0=makeQuery(id+"F34.imprint","IMPRINT",FACE,{"disambiguationData":[TD([[makeQuery(id+"F34.imprint","IMPRINT",EDGE,{"derivedFrom":sQuery(id+"F34.wireOp",EDGE,"E97")}),1.0]])]});
            extrude(context, id + "F35", {"entities" : qUnion([Q0]), "operationType" : NewBodyOperationType.REMOVE, "oppositeDirection" : true, "depth" : 4 * mm});
        }
        {
            var Q0;
            Q0=makeQuery(id+"F34.imprint","IMPRINT",FACE,{"disambiguationData":[TD([[makeQuery(id+"F34.imprint","IMPRINT",EDGE,{"derivedFrom":sQuery(id+"F34.wireOp",EDGE,"E98")}),1.0]])]});
            extrude(context, id + "F36", {"entities" : qUnion([Q0]), "operationType" : NewBodyOperationType.REMOVE, "oppositeDirection" : true, "depth" : 4 * mm});
        }
        {
            var Q0;
            Q0=makeQuery(id+"F5.boolean.opBoolean","MERGE",FACE,{"derivedFrom":[makeQuery(id+"F3.boolean.opBoolean","MERGE",FACE,{"derivedFrom":[makeQuery(id+"F1.opExtrude","SWEPT_FACE",FACE,{"disambiguationData":[OSD([sQuery(id+"F0.wireOp",EDGE,"E0.top")])]}),makeQuery(id+"F3.opExtrude","SWEPT_FACE",FACE,{"disambiguationData":[OSD([sQuery(id+"F2.wireOp",EDGE,"E7")])]})]}),makeQuery(id+"F5.opExtrude","SWEPT_FACE",FACE,{"disambiguationData":[OSD([sQuery(id+"F4.wireOp",EDGE,"E16.0")])]})]});
            var sketch = newSketch(context, id + "F37", { "sketchPlane" : qUnion([Q0])});
            skText(sketch, "E99", { "text": "X16 v0.1", "fontName": "OpenSans-Regular.ttf"});
            const initialGuessF37  = {"E99": [-0.0358, 0.00103, 1, 0, 0.00482]};
            skSetInitialGuess(sketch, initialGuessF37);
            skSolve(sketch);
        }
        {
            var Q0;
            Q0 = qSketchRegion(id + "F37", true);
            extrude(context, id + "F38", {"entities" : qUnion([Q0]), "operationType" : NewBodyOperationType.REMOVE, "oppositeDirection" : true, "depth" : .5 * mm});
        }
    });
